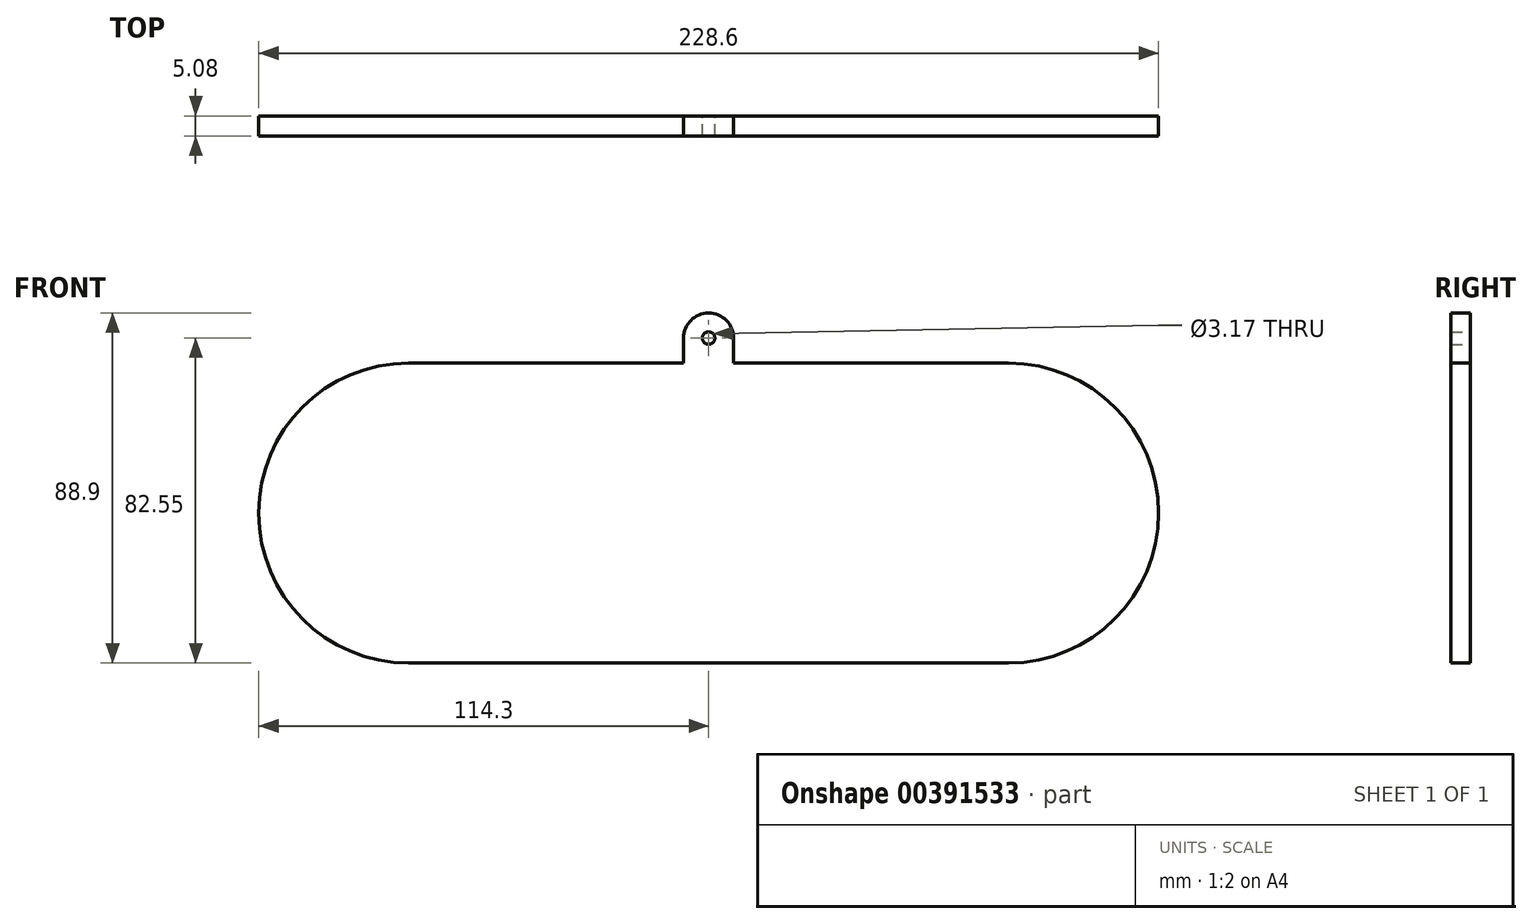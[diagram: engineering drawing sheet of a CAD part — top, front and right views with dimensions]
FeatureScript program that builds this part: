
annotation { "Feature Type Name" : "Feature", "Feature Type Description" : "" }
export const myFeature = defineFeature(function(context is Context, id is Id, definition is map)
    precondition{}
    {
        {
            var Q0;
            Q0=qCreatedBy(makeId("Front.planeOp"),FACE);
            var sketch = newSketch(context, id + "F0", { "sketchPlane" : qUnion([Q0])});
            skLineSegment(sketch, "E0.bottom", {"start": v(-76.2, 38.1) * mm, "end": v(76.2, 38.1) * mm});
            skLineSegment(sketch, "E0.top", {"start": v(-76.2, -38.1) * mm, "end": v(76.2, -38.1) * mm});
            skLineSegment(sketch, "E0.left", {"start": v(-76.2, 38.1) * mm, "end": v(-76.2, -38.1) * mm});
            skLineSegment(sketch, "E0.right", {"start": v(76.2, 38.1) * mm, "end": v(76.2, -38.1) * mm});
            skPoint(sketch, "E0.middle", {"position": v(0, 0) * mm});
            skCircle(sketch, "E1", {"center": v(-76.2, 0) * mm, "radius": 38.1 * mm});
            skCircle(sketch, "E2", {"center": v(76.2, 0) * mm, "radius": 38.1 * mm});
            skLineSegment(sketch, "E3", {"start": v(-6.35, 38.1) * mm, "end": v(-6.35, 44.45) * mm});
            skLineSegment(sketch, "E4", {"start": v(-6.35, 44.45) * mm, "end": v(6.35, 44.45) * mm});
            skLineSegment(sketch, "E5", {"start": v(6.35, 44.45) * mm, "end": v(6.35, 38.1) * mm});
            skCircle(sketch, "E6", {"center": v(0, 44.45) * mm, "radius": 6.35 * mm});
            skCircle(sketch, "E7", {"center": v(0, 44.45) * mm, "radius": 1.59 * mm});
            skSolve(sketch);
        }
        {
            var Q0;
            Q0 = qSketchRegion(id + "F0", true);
            extrude(context, id + "F1", {"entities" : qUnion([Q0]), "depth" : 5.08 * mm, "offsetDistance" : 25.4 * mm});
        }
    });
